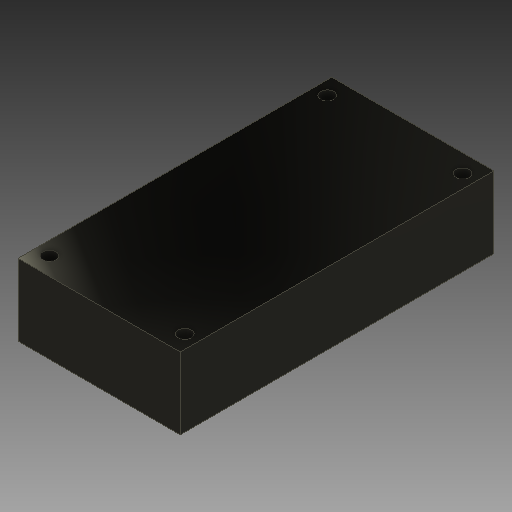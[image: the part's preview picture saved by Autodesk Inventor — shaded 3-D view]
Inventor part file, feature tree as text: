
AUTODESK INVENTOR PART (.ipt)
format: ipt  version: 2020 (Build 240168000, 168)  size: 107,520 bytes
history: native  units: mm
features: other x1, extrude x1, sketch x1
ambient origin geometry x8: Origin, YZ Plane, XZ Plane, XY Plane, X Axis, Y Axis, Z Axis, Center Point
bodies: Body1 (feature_tree)
feature tree (3):
  other  "Твердое тело1"
  extrude  "Выдавливание1"  Depth=36.2mm
  sketch  "Эскиз1"
